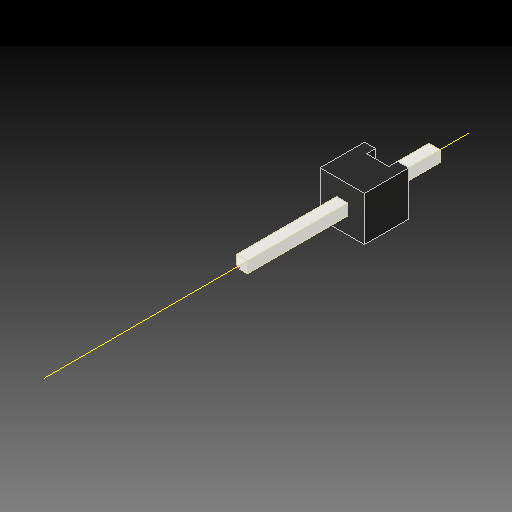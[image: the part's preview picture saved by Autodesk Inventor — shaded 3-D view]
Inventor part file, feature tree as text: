
AUTODESK INVENTOR PART (.ipt)
format: ipt  version: 2020 (Build 240168000, 168)  size: 115,712 bytes
history: native  units: mm
features: other x2, sketch x1
ambient origin geometry x8: Origin, YZ Plane, XZ Plane, XY Plane, X Axis, Y Axis, Z Axis, Center Point
bodies: Solid1 (feature_tree), Solid2 (feature_tree), Body (feature_tree)
feature tree (3):
  sketch  "Sketch1"
  other  "Work Axis2"
  other  "Pin"
